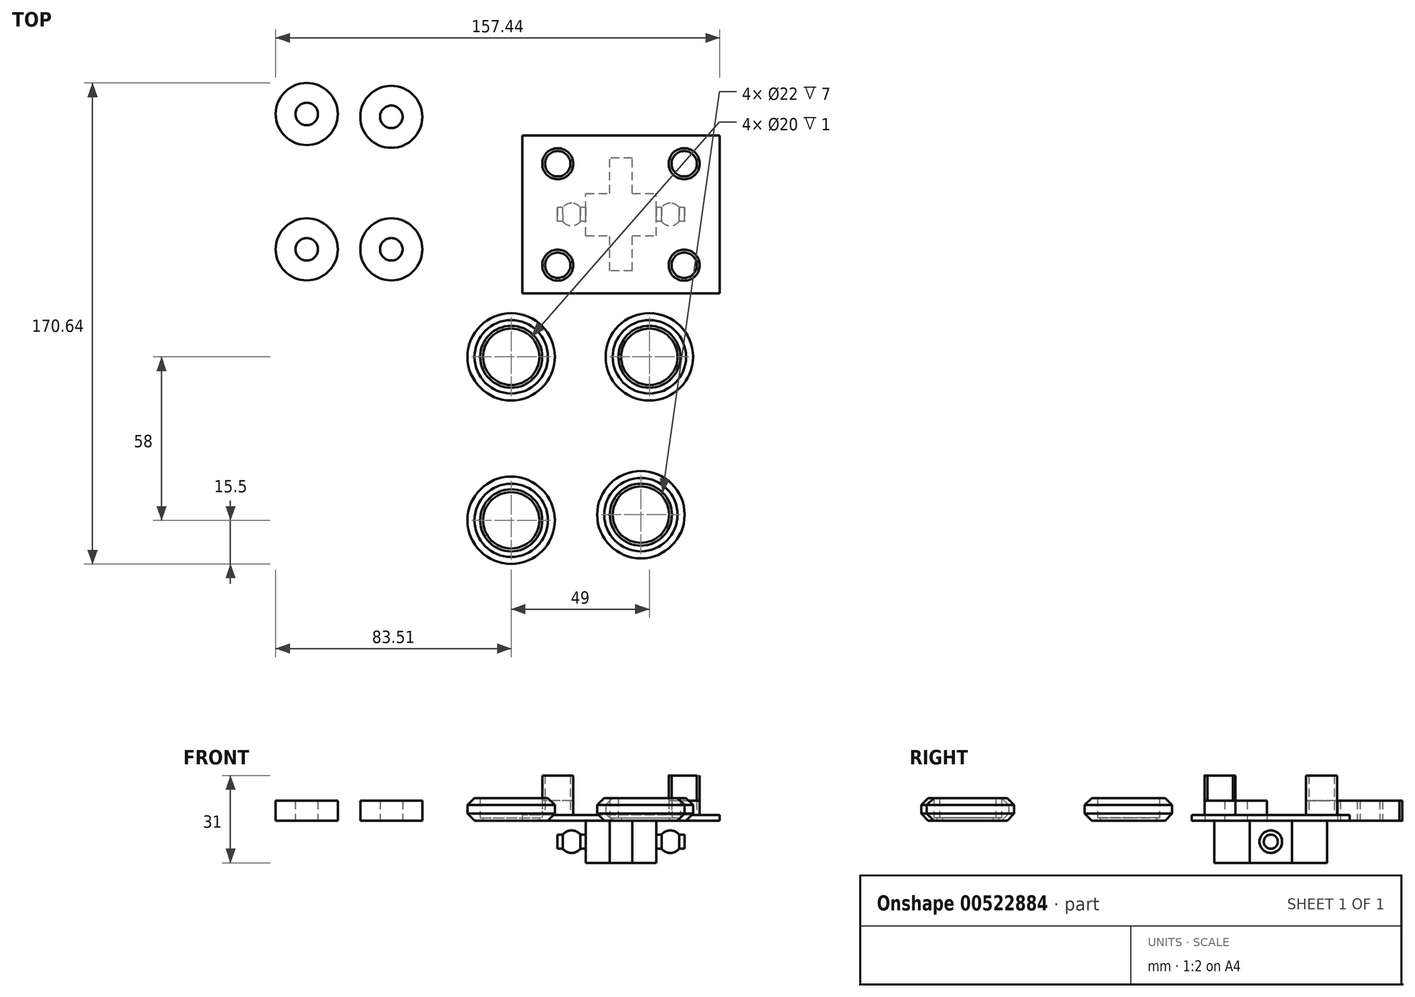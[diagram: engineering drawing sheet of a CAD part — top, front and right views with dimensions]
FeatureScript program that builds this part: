
annotation { "Feature Type Name" : "Feature", "Feature Type Description" : "" }
export const myFeature = defineFeature(function(context is Context, id is Id, definition is map)
    precondition{}
    {
        {
            var Q0;
            Q0=qCreatedBy(makeId("Right.planeOp"),FACE);
            var sketch = newSketch(context, id + "F0", { "sketchPlane" : qUnion([Q0])});
            skLineSegment(sketch, "E0", {"start": v(0, 0) * mm, "end": v(2, 0) * mm});
            skLineSegment(sketch, "E1", {"start": v(2, 0) * mm, "end": v(6, 4) * mm});
            skLineSegment(sketch, "E2", {"start": v(6, 4) * mm, "end": v(2, 8) * mm});
            skLineSegment(sketch, "E3", {"start": v(2, 8) * mm, "end": v(0, 8) * mm});
            skLineSegment(sketch, "E4", {"start": v(0, 8) * mm, "end": v(0, 0) * mm});
            skLineSegment(sketch, "E5", {"start": v(-11, 0) * mm, "end": v(-11, 5.99) * mm});
            skLineSegment(sketch, "E6.bottom", {"start": v(0, 1) * mm, "end": v(-1, 1) * mm});
            skLineSegment(sketch, "E6.top", {"start": v(0, 0) * mm, "end": v(-1, 0) * mm});
            skLineSegment(sketch, "E6.left", {"start": v(0, 1) * mm, "end": v(0, 0) * mm});
            skLineSegment(sketch, "E6.right", {"start": v(-1, 1) * mm, "end": v(-1, 0) * mm});
            skLineSegment(sketch, "E7", {"start": v(4.5, 5.5) * mm, "end": v(4.5, 2.5) * mm});
            skSolve(sketch);
        }
        {
            var Q0;
            {var subQ4=sQuery(id+"F0.wireOp",EDGE,"E0");Q0=makeQuery(id+"F0.imprint","IMPRINT",FACE,{"disambiguationData":[TD([[makeQuery(id+"F0.imprint","IMPRINT",EDGE,{"derivedFrom":subQ4}),1.0]])]});}
            var Q1;
            Q1=makeQuery(id+"F0.imprint","IMPRINT",FACE,{"disambiguationData":[TD([[makeQuery(id+"F0.imprint","IMPRINT",EDGE,{"derivedFrom":sQuery(id+"F0.wireOp",EDGE,"E6.bottom")}),1.0]])]});
            var Q2;
            Q2=sQuery(id+"F0.wireOp",EDGE,"E5");
            revolve(context, id + "F1", {"entities" : qUnion([Q0, Q1]), "axis" : qUnion([Q2]), "revolveType" : RevolveType.FULL});
        }
        {
            var Q0;
            Q0=qCreatedBy(makeId("Top.planeOp"),FACE);
            var sketch = newSketch(context, id + "F2", { "sketchPlane" : qUnion([Q0])});
            skCircle(sketch, "E8", {"center": v(-42.5, 27.14) * mm, "radius": 11 * mm});
            skCircle(sketch, "E9", {"center": v(-42.5, 27.14) * mm, "radius": 4 * mm});
            skSolve(sketch);
        }
        {
            var Q0;
            Q0=qSketchRegion(id+"F2",true);
            extrude(context, id + "F3", {"entities" : qUnion([Q0]), "depth" : 7 * mm});
        }
        {
            var Q0;
            Q0=qCreatedBy(makeId("Top.planeOp"),FACE);
            var sketch = newSketch(context, id + "F4", { "sketchPlane" : qUnion([Q0])});
            skLineSegment(sketch, "E10.bottom", {"start": v(73.93, 11.5) * mm, "end": v(3.93, 11.5) * mm});
            skLineSegment(sketch, "E10.top", {"start": v(73.93, 67.5) * mm, "end": v(3.93, 67.5) * mm});
            skLineSegment(sketch, "E10.left", {"start": v(73.93, 11.5) * mm, "end": v(73.93, 67.5) * mm});
            skLineSegment(sketch, "E10.right", {"start": v(3.93, 11.5) * mm, "end": v(3.93, 67.5) * mm});
            skSolve(sketch);
        }
        {
            var Q0;
            Q0=qSketchRegion(id+"F4",true);
            extrude(context, id + "F5", {"entities" : qUnion([Q0]), "depth" : 2 * mm});
        }
        {
            var Q0;
            Q0=makeQuery(id+"F5.opExtrude","CAP_FACE",FACE,{"disambiguationData":[OSD([sQuery(id+"F4.wireOp",EDGE,"E10.bottom"),sQuery(id+"F4.wireOp",EDGE,"E10.top"),sQuery(id+"F4.wireOp",EDGE,"E10.left"),sQuery(id+"F4.wireOp",EDGE,"E10.right")])],"isStart":false});
            var sketch = newSketch(context, id + "F6", { "sketchPlane" : qUnion([Q0])});
            skLineSegment(sketch, "E11", {"start": v(38.93, 11.5) * mm, "end": v(38.93, 67.5) * mm});
            skLineSegment(sketch, "E12", {"start": v(3.93, 39.5) * mm, "end": v(73.93, 39.5) * mm});
            skCircle(sketch, "E13", {"center": v(61.35, 21.5) * mm, "radius": 5.5 * mm});
            skCircle(sketch, "E14", {"center": v(61.35, 21.5) * mm, "radius": 4.5 * mm});
            skCircle(sketch, "E15.MirrorC", {"center": v(16.5, 21.5) * mm, "radius": 5.5 * mm});
            skCircle(sketch, "E16.MirrorC", {"center": v(16.5, 21.5) * mm, "radius": 4.5 * mm});
            skLineSegment(sketch, "E17.MirrorCS", {"start": v(73.93, 39.5) * mm, "end": v(3.93, 39.5) * mm});
            skCircle(sketch, "E18.MirrorC", {"center": v(61.35, 57.5) * mm, "radius": 4.5 * mm});
            skCircle(sketch, "E19.MirrorC", {"center": v(61.35, 57.5) * mm, "radius": 5.5 * mm});
            skCircle(sketch, "E20.MirrorC", {"center": v(16.5, 57.5) * mm, "radius": 5.5 * mm});
            skCircle(sketch, "E21.MirrorC", {"center": v(16.5, 57.5) * mm, "radius": 4.5 * mm});
            skSolve(sketch);
        }
        {
            var Q0;
            Q0=makeQuery(id+"F6.imprint","IMPRINT",FACE,{"disambiguationData":[TD([[makeQuery(id+"F6.imprint","IMPRINT",EDGE,{"derivedFrom":sQuery(id+"F6.wireOp",EDGE,"E14")}),1.0]])]});
            var Q1;
            Q1=makeQuery(id+"F6.imprint","IMPRINT",FACE,{"disambiguationData":[TD([[makeQuery(id+"F6.imprint","IMPRINT",EDGE,{"derivedFrom":sQuery(id+"F6.wireOp",EDGE,"E16.MirrorC")}),-1.0]])]});
            var Q2;
            Q2=makeQuery(id+"F6.imprint","IMPRINT",FACE,{"disambiguationData":[TD([[makeQuery(id+"F6.imprint","IMPRINT",EDGE,{"derivedFrom":sQuery(id+"F6.wireOp",EDGE,"E21.MirrorC")}),1.0]])]});
            var Q3;
            Q3=makeQuery(id+"F6.imprint","IMPRINT",FACE,{"disambiguationData":[TD([[makeQuery(id+"F6.imprint","IMPRINT",EDGE,{"derivedFrom":sQuery(id+"F6.wireOp",EDGE,"E18.MirrorC")}),-1.0]])]});
            extrude(context, id + "F7", {"entities" : qUnion([Q0, Q1, Q2, Q3]), "operationType" : NewBodyOperationType.ADD, "depth" : 14 * mm, "offsetDistance" : 25 * mm});
        }
        {
            var Q0;
            Q0=qSketchRegion(id+"F6",true);
            extrude(context, id + "F8", {"entities" : qUnion([Q0]), "operationType" : NewBodyOperationType.ADD, "depth" : 5 * mm});
        }
        {
            var Q0;
            Q0=makeQuery(id+"F3.opExtrude","SWEPT_BODY",BODY,{"disambiguationData":[OSD([sQuery(id+"F2.wireOp",EDGE,"E8"),sQuery(id+"F2.wireOp",EDGE,"E9")])]});
            transform(context, id + "F9", {"entities" : qUnion([Q0]), "transformType" : TransformType.TRANSLATION_3D, "dx" : 0 * mm, "dy" : 47 * mm, "dz" : 0 * mm, "makeCopy" : true});
        }
        {
            var Q0;
            Q0=makeQuery(id+"F3.opExtrude","SWEPT_BODY",BODY,{"disambiguationData":[OSD([sQuery(id+"F2.wireOp",EDGE,"E8"),sQuery(id+"F2.wireOp",EDGE,"E9")])]});
            transform(context, id + "F10", {"entities" : qUnion([Q0]), "transformType" : TransformType.TRANSLATION_3D, "dx" : -30 * mm, "dy" : 0 * mm, "dz" : 0 * mm, "makeCopy" : true});
        }
        {
            var Q0;
            Q0=makeQuery(id+"F10.opPattern","COPY",BODY,{"derivedFrom":makeQuery(id+"F3.opExtrude","SWEPT_BODY",BODY,{"disambiguationData":[OSD([sQuery(id+"F2.wireOp",EDGE,"E8"),sQuery(id+"F2.wireOp",EDGE,"E9")])]}),"instanceName":"1"});
            transform(context, id + "F11", {"entities" : qUnion([Q0]), "transformType" : TransformType.TRANSLATION_3D, "dx" : 0 * mm, "dy" : 48 * mm, "dz" : 0 * mm, "makeCopy" : true});
        }
        {
            var Q0;
            Q0=makeQuery(id+"F1.opRevolve","SWEPT_BODY",BODY,{"disambiguationData":[OSD([sQuery(id+"F0.wireOp",EDGE,"E0"),sQuery(id+"F0.wireOp",EDGE,"E1"),sQuery(id+"F0.wireOp",EDGE,"E2"),sQuery(id+"F0.wireOp",EDGE,"E3"),sQuery(id+"F0.wireOp",EDGE,"E4"),sQuery(id+"F0.wireOp",EDGE,"E6.bottom"),sQuery(id+"F0.wireOp",EDGE,"E6.top"),sQuery(id+"F0.wireOp",EDGE,"E6.right"),sQuery(id+"F0.wireOp",EDGE,"E7")])]});
            transform(context, id + "F12", {"entities" : qUnion([Q0]), "transformType" : TransformType.TRANSLATION_3D, "dx" : 49 * mm, "dy" : 0 * mm, "dz" : 0 * mm, "makeCopy" : true});
        }
        {
            var Q0;
            Q0=makeQuery(id+"F1.opRevolve","SWEPT_BODY",BODY,{"disambiguationData":[OSD([sQuery(id+"F0.wireOp",EDGE,"E0"),sQuery(id+"F0.wireOp",EDGE,"E1"),sQuery(id+"F0.wireOp",EDGE,"E2"),sQuery(id+"F0.wireOp",EDGE,"E3"),sQuery(id+"F0.wireOp",EDGE,"E4"),sQuery(id+"F0.wireOp",EDGE,"E6.bottom"),sQuery(id+"F0.wireOp",EDGE,"E6.top"),sQuery(id+"F0.wireOp",EDGE,"E6.right"),sQuery(id+"F0.wireOp",EDGE,"E7")])]});
            transform(context, id + "F13", {"entities" : qUnion([Q0]), "transformType" : TransformType.TRANSLATION_3D, "dx" : 46 * mm, "dy" : -56 * mm, "dz" : 0 * mm, "makeCopy" : true});
        }
        {
            var Q0;
            Q0=makeQuery(id+"F1.opRevolve","SWEPT_BODY",BODY,{"disambiguationData":[OSD([sQuery(id+"F0.wireOp",EDGE,"E0"),sQuery(id+"F0.wireOp",EDGE,"E1"),sQuery(id+"F0.wireOp",EDGE,"E2"),sQuery(id+"F0.wireOp",EDGE,"E3"),sQuery(id+"F0.wireOp",EDGE,"E4"),sQuery(id+"F0.wireOp",EDGE,"E6.bottom"),sQuery(id+"F0.wireOp",EDGE,"E6.top"),sQuery(id+"F0.wireOp",EDGE,"E6.right"),sQuery(id+"F0.wireOp",EDGE,"E7")])]});
            transform(context, id + "F14", {"entities" : qUnion([Q0]), "transformType" : TransformType.TRANSLATION_3D, "dx" : 0 * mm, "dy" : -58 * mm, "dz" : 0 * mm, "makeCopy" : true});
        }
        {
            var Q0;
            Q0=makeQuery(id+"F5.opExtrude","CAP_FACE",FACE,{"disambiguationData":[OSD([sQuery(id+"F4.wireOp",EDGE,"E10.bottom"),sQuery(id+"F4.wireOp",EDGE,"E10.top"),sQuery(id+"F4.wireOp",EDGE,"E10.left"),sQuery(id+"F4.wireOp",EDGE,"E10.right")])],"isStart":true});
            var sketch = newSketch(context, id + "F15", { "sketchPlane" : qUnion([Q0])});
            skLineSegment(sketch, "E22.bottom", {"start": v(26.43, -32) * mm, "end": v(51.43, -32) * mm});
            skLineSegment(sketch, "E22.top", {"start": v(26.43, -47) * mm, "end": v(51.43, -47) * mm});
            skLineSegment(sketch, "E22.left", {"start": v(26.43, -32) * mm, "end": v(26.43, -47) * mm});
            skLineSegment(sketch, "E22.right", {"start": v(51.43, -32) * mm, "end": v(51.43, -47) * mm});
            skPoint(sketch, "E22.middle", {"position": v(38.93, -39.5) * mm});
            skPoint(sketch, "E22.middle.positionSnap0", {"position": v(38.93, -67.5) * mm});
            skPoint(sketch, "E22.middle.positionSnap1", {"position": v(3.93, -39.5) * mm});
            skPoint(sketch, "E22.centerSnap0", {"position": v(38.93, -67.5) * mm});
            skPoint(sketch, "E22.centerSnap1", {"position": v(3.93, -39.5) * mm});
            skLineSegment(sketch, "E23.bottom", {"start": v(42.93, -19.5) * mm, "end": v(34.93, -19.5) * mm});
            skLineSegment(sketch, "E23.top", {"start": v(42.93, -59.5) * mm, "end": v(34.93, -59.5) * mm});
            skLineSegment(sketch, "E23.left", {"start": v(42.93, -19.5) * mm, "end": v(42.93, -59.5) * mm});
            skLineSegment(sketch, "E23.right", {"start": v(34.93, -19.5) * mm, "end": v(34.93, -59.5) * mm});
            skSolve(sketch);
        }
        {
            var Q0;
            Q0=makeQuery(id+"F15.imprint","IMPRINT",FACE,{"disambiguationData":[TD([[makeQuery(id+"F15.imprint","IMPRINT",EDGE,{"derivedFrom":sQuery(id+"F15.wireOp",EDGE,"E22.bottom")}),-1.0]])]});
            var Q1;
            {var subQ5=sQuery(id+"F15.wireOp",EDGE,"E23.bottom");Q1=makeQuery(id+"F15.imprint","IMPRINT",FACE,{"disambiguationData":[TD([[makeQuery(id+"F15.imprint","IMPRINT",EDGE,{"derivedFrom":subQ5}),1.0]])]});}
            var Q2;
            {var subQ5=sQuery(id+"F15.wireOp",EDGE,"E23.top");Q2=makeQuery(id+"F15.imprint","IMPRINT",FACE,{"disambiguationData":[TD([[makeQuery(id+"F15.imprint","IMPRINT",EDGE,{"derivedFrom":subQ5}),-1.0]])]});}
            extrude(context, id + "F16", {"entities" : qUnion([Q0, Q1, Q2]), "operationType" : NewBodyOperationType.ADD, "depth" : 15 * mm, "offsetDistance" : 25 * mm});
        }
        {
            var Q0;
            Q0=makeQuery(id+"F16.opExtrude","SWEPT_FACE",FACE,{"disambiguationData":[OSD([sQuery(id+"F15.wireOp",EDGE,"E22.left")])]});
            var sketch = newSketch(context, id + "F17", { "sketchPlane" : qUnion([Q0])});
            skCircle(sketch, "E24", {"center": v(-39.5, -7.5) * mm, "radius": 2.5 * mm});
            skPoint(sketch, "E24.centerSnap0", {"position": v(-32, -7.5) * mm});
            skPoint(sketch, "E24.centerSnap1", {"position": v(-39.5, -15) * mm});
            skSolve(sketch);
        }
        {
            var Q0;
            Q0 = qSketchRegion(id + "F17", true);
            extrude(context, id + "F18", {"entities" : qUnion([Q0]), "operationType" : NewBodyOperationType.REMOVE, "oppositeDirection" : true, "depth" : 30 * mm, "offsetDistance" : 25 * mm});
        }
        {
            var Q0;
            Q0=makeQuery(id+"F17.imprint","IMPRINT",FACE,{"disambiguationData":[TD([[makeQuery(id+"F17.imprint","IMPRINT",EDGE,{"derivedFrom":sQuery(id+"F17.wireOp",EDGE,"E24")}),1.0]])]});
            extrude(context, id + "F19", {"entities" : qUnion([Q0]), "oppositeDirection" : true, "depth" : 35 * mm, "offsetDistance" : 25 * mm});
        }
        {
            var Q0;
            Q0=makeQuery(id+"F17.imprint","IMPRINT",FACE,{"disambiguationData":[TD([[makeQuery(id+"F17.imprint","IMPRINT",EDGE,{"derivedFrom":sQuery(id+"F17.wireOp",EDGE,"E24")}),1.0]])]});
            extrude(context, id + "F20", {"entities" : qUnion([Q0]), "operationType" : NewBodyOperationType.ADD, "depth" : 10 * mm, "offsetDistance" : 25 * mm});
        }
        {
            var Q0;
            Q0=makeQuery(id+"F16.opExtrude","SWEPT_FACE",FACE,{"disambiguationData":[OSD([sQuery(id+"F15.wireOp",EDGE,"E22.bottom")])]});
            var sketch = newSketch(context, id + "F21", { "sketchPlane" : qUnion([Q0])});
            skLineSegment(sketch, "E25.bottom", {"start": v(18.43, -4.43) * mm, "end": v(21.43, -4.43) * mm});
            skLineSegment(sketch, "E25.top", {"start": v(18.43, -11.43) * mm, "end": v(21.43, -11.43) * mm});
            skLineSegment(sketch, "E25.left", {"start": v(18.43, -4.43) * mm, "end": v(18.43, -11.43) * mm});
            skLineSegment(sketch, "E25.right", {"start": v(21.43, -4.43) * mm, "end": v(21.43, -11.43) * mm});
            skLineSegment(sketch, "E26.bottom", {"start": v(56.43, -4.15) * mm, "end": v(59.43, -4.15) * mm});
            skLineSegment(sketch, "E26.top", {"start": v(56.43, -12.15) * mm, "end": v(59.43, -12.15) * mm});
            skLineSegment(sketch, "E26.left", {"start": v(56.43, -4.15) * mm, "end": v(56.43, -12.15) * mm});
            skLineSegment(sketch, "E26.right", {"start": v(59.43, -4.15) * mm, "end": v(59.43, -12.15) * mm});
            skSolve(sketch);
        }
        {
            var Q0;
            Q0 = qSketchRegion(id + "F21", true);
            extrude(context, id + "F22", {"entities" : qUnion([Q0]), "operationType" : NewBodyOperationType.REMOVE, "oppositeDirection" : true, "depth" : 7.5 * mm, "offsetDistance" : 25 * mm});
        }
        {
            var Q0;
            Q0=makeQuery(id+"F22.boolean.opBoolean","COPY",FACE,{"derivedFrom":makeQuery(id+"F22.opExtrude","CAP_FACE",FACE,{"disambiguationData":[OSD([sQuery(id+"F21.wireOp",EDGE,"E25.bottom"),sQuery(id+"F21.wireOp",EDGE,"E25.top"),sQuery(id+"F21.wireOp",EDGE,"E25.left"),sQuery(id+"F21.wireOp",EDGE,"E25.right")])],"isStart":false})});
            var sketch = newSketch(context, id + "F23", { "sketchPlane" : qUnion([Q0])});
            skCircle(sketch, "E27", {"center": v(21.43, -7.5) * mm, "radius": 4 * mm});
            skCircle(sketch, "E28", {"center": v(56.43, -7.5) * mm, "radius": 4 * mm});
            skLineSegment(sketch, "E29", {"start": v(21.43, -3.5) * mm, "end": v(21.43, -11.5) * mm});
            skLineSegment(sketch, "E30", {"start": v(56.43, -3.5) * mm, "end": v(56.43, -11.5) * mm});
            skSolve(sketch);
        }
        {
            var Q0;
            {var subQ1=sQuery(id+"F21.wireOp",EDGE,"E25.left");Q0=makeQuery(id+"F23.imprint","IMPRINT",FACE,{"disambiguationData":[TD([[makeQuery(id+"F23.imprint","IMPRINT",EDGE,{"derivedFrom":makeQuery(id+"F22.boolean.opBoolean","COPY",EDGE,{"derivedFrom":makeQuery(id+"F22.opExtrude","CAP_EDGE",EDGE,{"disambiguationData":[OSD([subQ1])],"isStart":false})})}),1.0]])]});}
            var Q1;
            {var subQ0=sQuery(id+"F21.wireOp",EDGE,"E25.left");Q1=makeQuery(id+"F23.imprint","IMPRINT",FACE,{"disambiguationData":[TD([[makeQuery(id+"F23.imprint","IMPRINT",EDGE,{"derivedFrom":makeQuery(id+"F22.boolean.opBoolean","COPY",EDGE,{"derivedFrom":makeQuery(id+"F22.opExtrude","CAP_EDGE",EDGE,{"disambiguationData":[OSD([subQ0])],"isStart":false})})}),-1.0]])]});}
            var Q2;
            Q2=sQuery(id+"F23.wireOp",EDGE,"E29");
            revolve(context, id + "F24", {"operationType" : NewBodyOperationType.ADD, "entities" : qUnion([Q0, Q1]), "axis" : qUnion([Q2]), "revolveType" : RevolveType.FULL});
        }
        {
            var Q0;
            {var subQ0=sQuery(id+"F23.wireOp",EDGE,"E30");Q0=makeQuery(id+"F23.imprint","IMPRINT",FACE,{"disambiguationData":[TD([[makeQuery(id+"F23.imprint","IMPRINT",EDGE,{"derivedFrom":subQ0}),1.0]])]});}
            var Q1;
            Q1=sQuery(id+"F23.wireOp",EDGE,"E30");
            revolve(context, id + "F25", {"operationType" : NewBodyOperationType.ADD, "entities" : qUnion([Q0]), "axis" : qUnion([Q1]), "revolveType" : RevolveType.FULL});
        }
    });
